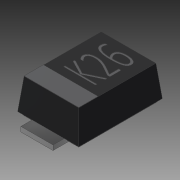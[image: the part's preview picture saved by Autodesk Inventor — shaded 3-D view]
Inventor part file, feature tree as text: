
AUTODESK INVENTOR PART (.ipt)
format: ipt  version: 2016 (Build 200138000, 138)  size: 284,672 bytes
history: native  units: mm
features: extrude x5, sketch x4, projected_geometry x4, plane x1
ambient origin geometry x8: Origin, YZ Plane, XZ Plane, XY Plane, X Axis, Y Axis, Z Axis, Center Point
bodies: Body1 (feature_tree)
feature tree (14):
  extrude  "Extrusion4"  Depth=1.05mm
  extrude  "Extrusion5"  Depth=0.1mm
  sketch  "Sketch13"  dims[d13=0.05mm d14=0.1mm]
  extrude  "Extrusion6"  Depth=0.1mm
  extrude  "Extrusion7"  Depth=0.1mm
  plane  "Work Plane1"
  extrude  "Extrusion8"  Depth=2.3mm TaperAngle=0.0deg
  sketch  "Sketch10"  dims[d8=2.6mm d9=1.05mm]
  sketch  "Sketch11"  dims[d10=0.1mm d12=0.04mm]
  projected_geometry  "Projected Loop1"
  projected_geometry  "Projected Loop2"
  projected_geometry  "Projected Loop3"
  sketch  "Sketch14"  dims[d15=1.9mm d16=0.0mm d18=0.1mm d20=4.74mm d21=0.0mm d22=0.04mm d23=0.05mm d24=0.15mm d26=0.6mm d27=0.01mm d28=0.0mm d29=0.01mm d30=0.0mm d31=0.05mm d32=3.3mm d33=1.0mm d34=2.3mm d35=0.01mm d36=0.0mm]
  projected_geometry  "Projected Loop4"
